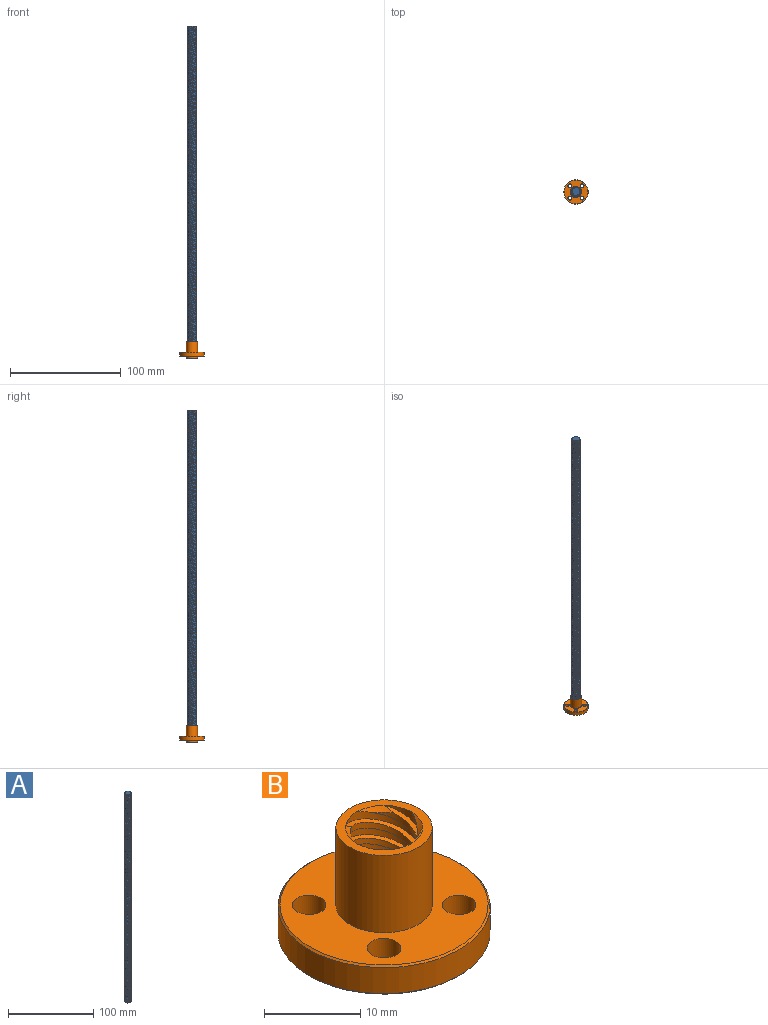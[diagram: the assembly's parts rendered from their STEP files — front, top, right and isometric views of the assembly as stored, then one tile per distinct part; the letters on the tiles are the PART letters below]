
ASSEMBLY  parts=2 mates=1
PART A: 26 faces, bbox 2094x2094x581.3 mm
  f0: cone r=4mm half-angle=45deg, axis (0,0,1), area 2.4mm2, adj f3,f19,f20,f23
  f1: cylinder r=4mm len=299mm, axis (0,0,-1), area 943.4mm2, adj f5,f6,f8,f9
  f2: cone r=3.5mm half-angle=45deg, axis (0,0,-1), area 2.3mm2, adj f3,f18,f19,f23
  f3: bspline ~301.13x8mm, area 482.1mm2, adj f0,f2,f4,f19
  f4: cylinder r=3.5mm len=300mm, axis (0,0,1), area 792.2mm2, adj f3,f5,f18,f20
  f5: bspline ~1051.52x581.26mm, area 480.4mm2, adj f1,f4,f6,f8
  f6: cone r=4mm half-angle=45deg, axis (0,0,1), area 2.4mm2, adj f1,f5,f9,f20
  f7: cylinder r=4mm len=299mm, axis (0,0,-1), area 943.4mm2, adj f11,f12,f14,f15
  f8: cone r=3.5mm half-angle=45deg, axis (0,0,-1), area 2.3mm2, adj f1,f5,f9,f18
  f9: bspline ~301.13x8mm, area 482.1mm2, adj f1,f6,f8,f10
  f10: cylinder r=3.5mm len=300mm, axis (0,0,1), area 792.2mm2, adj f9,f11,f18,f20
  f11: bspline ~1051.52x581.26mm, area 480.4mm2, adj f7,f10,f12,f14
  f12: cone r=4mm half-angle=45deg, axis (0,0,1), area 2.4mm2, adj f7,f11,f15,f20
  f13: cylinder r=4mm len=299mm, axis (0,0,-1), area 943.4mm2, adj f17,f22,f24,f25
  f14: cone r=3.5mm half-angle=45deg, axis (0,0,-1), area 2.3mm2, adj f7,f11,f15,f18
  f15: bspline ~301.13x8mm, area 482.1mm2, adj f7,f12,f14,f16
  f16: cylinder r=3.5mm len=300mm, axis (0,0,1), area 792.2mm2, adj f15,f17,f18,f20
  f17: bspline ~1051.52x581.26mm, area 480.4mm2, adj f13,f16,f24,f25
  f18: plane 7x7mm, normal (0,0,1), area 38.5mm2, adj f2,f4,f8,f10,f14,f16,f21,f24
  f19: cylinder r=4mm len=299mm, axis (0,0,-1), area 943.4mm2, adj f0,f2,f3,f23
  f20: plane 7x7mm, normal (0,0,-1), area 38.5mm2, adj f0,f4,f6,f10,f12,f16,f21,f25
  f21: cylinder r=3.5mm len=300mm, axis (0,0,1), area 792.2mm2, adj f18,f20,f22,f23
  f22: bspline ~301.13x8mm, area 482.1mm2, adj f13,f21,f24,f25
  f23: bspline ~1051.52x581.26mm, area 480.4mm2, adj f0,f2,f19,f21
  f24: cone r=3.5mm half-angle=45deg, axis (0,0,-1), area 2.3mm2, adj f13,f17,f18,f22
  f25: cone r=4mm half-angle=45deg, axis (0,0,1), area 2.4mm2, adj f13,f17,f20,f22
PART B: 37 faces, bbox 22x22x16.4 mm
  f0: cylinder r=1.75mm len=3.7mm, axis (0,0,-1), area 40.7mm2, adj f5,f6
  f1: cylinder r=1.75mm len=3.7mm, axis (0,0,-1), area 40.7mm2, adj f5,f6
  f2: cylinder r=1.75mm len=3.7mm, axis (0,0,-1), area 40.7mm2, adj f5,f6
  f3: cylinder r=1.75mm len=3.7mm, axis (0,0,-1), area 40.7mm2, adj f5,f6
  f4: cylinder r=11mm len=22mm, axis (0,0,-1), area 228.1mm2, adj f27,f28
  f5: plane 21.6x21.6mm, normal (0,0,1), area 249.4mm2, adj f0,f1,f2,f3,f9,f28
  f6: plane 21.6x21.6mm, normal (0,0,-1), area 249.4mm2, adj f0,f1,f2,f3,f8,f27
  f7: plane 10x10mm, normal (0,0,-1), area 28.3mm2, adj f8,f11,f15,f19,f23,f29,f30,f31
  f8: cylinder r=5mm len=10mm, axis (0,0,-1), area 47.1mm2, adj f6,f7
  f9: cylinder r=5mm len=10mm, axis (0,0,-1), area 307.9mm2, adj f5,f10
  f10: plane 10x10mm, normal (0,0,1), area 28.3mm2, adj f9,f11,f15,f19,f23,f33,f34,f35
  f11: cylinder r=4mm len=15mm, axis (0,0,-1), area 47.1mm2, adj f7,f10,f14,f16
  f12: bspline ~16.13x8mm, area 23.3mm2, adj f13,f23,f30,f36
  f13: cylinder r=3.5mm len=14mm, axis (0,0,1), area 28.2mm2, adj f12,f14,f30,f36
  f14: bspline ~16.4x9mm, area 23.3mm2, adj f11,f13,f30,f36
  f15: cylinder r=4mm len=15mm, axis (0,0,-1), area 47.1mm2, adj f7,f10,f18,f20
  f16: bspline ~16.13x8mm, area 23.3mm2, adj f11,f17,f29,f35
  f17: cylinder r=3.5mm len=14mm, axis (0,0,1), area 28.2mm2, adj f16,f18,f29,f35
  f18: bspline ~16.4x9mm, area 23.3mm2, adj f15,f17,f29,f35
  f19: cylinder r=4mm len=15mm, axis (0,0,-1), area 47.1mm2, adj f7,f10,f22,f25
  f20: bspline ~16.13x8mm, area 23.3mm2, adj f15,f21,f32,f34
  f21: cylinder r=3.5mm len=14mm, axis (0,0,1), area 28.2mm2, adj f20,f22,f32,f34
  f22: bspline ~16.4x9mm, area 23.3mm2, adj f19,f21,f32,f34
  f23: cylinder r=4mm len=15mm, axis (0,0,-1), area 47.1mm2, adj f7,f10,f12,f26
  f24: cylinder r=3.5mm len=14mm, axis (0,0,1), area 28.2mm2, adj f25,f26,f31,f33
  f25: bspline ~16.13x8mm, area 23.3mm2, adj f19,f24,f31,f33
  f26: bspline ~16.4x9mm, area 23.3mm2, adj f23,f24,f31,f33
  f27: cone r=11mm half-angle=45deg, axis (0,0,1), area 19.4mm2, adj f4,f6
  f28: cone r=10.8mm half-angle=45deg, axis (0,0,-1), area 19.4mm2, adj f4,f5
  f29: cone r=4mm half-angle=45deg, axis (0,0,-1), area 1.8mm2, adj f7,f16,f17,f18
  f30: cone r=4mm half-angle=45deg, axis (0,0,-1), area 1.8mm2, adj f7,f12,f13,f14
  f31: cone r=4mm half-angle=45deg, axis (0,0,-1), area 1.8mm2, adj f7,f24,f25,f26
  f32: cone r=4mm half-angle=45deg, axis (0,0,-1), area 1.8mm2, adj f7,f20,f21,f22
  f33: cone r=3.5mm half-angle=45deg, axis (0,0,1), area 1.8mm2, adj f10,f24,f25,f26
  f34: cone r=3.5mm half-angle=45deg, axis (0,0,1), area 1.8mm2, adj f10,f20,f21,f22
  f35: cone r=3.5mm half-angle=45deg, axis (0,0,1), area 1.8mm2, adj f10,f16,f17,f18
  f36: cone r=3.5mm half-angle=45deg, axis (0,0,1), area 1.8mm2, adj f10,f12,f13,f14
PLACE A t=(0,0,6.5)mm
PLACE B at identity fixed
MATE cylindrical A.f0 <-> B.f4  axis (0,0,-1) through (0,0,6.5)mm
